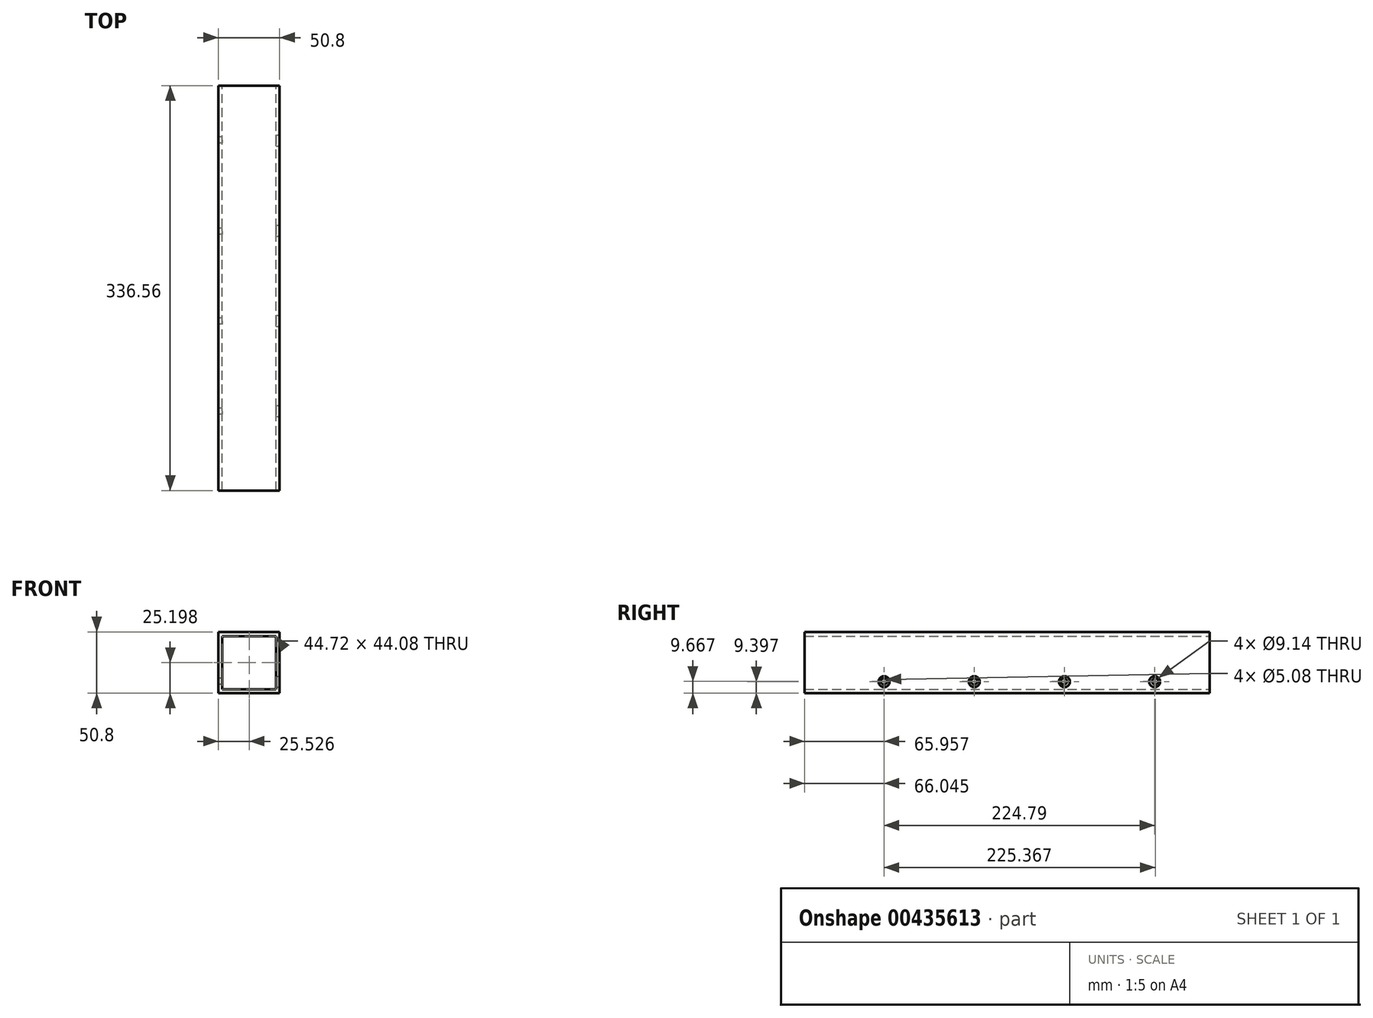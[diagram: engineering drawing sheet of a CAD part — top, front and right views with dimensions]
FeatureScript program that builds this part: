
annotation { "Feature Type Name" : "Feature", "Feature Type Description" : "" }
export const myFeature = defineFeature(function(context is Context, id is Id, definition is map)
    precondition{}
    {
        {
            var Q0;
            Q0=qCreatedBy(makeId("Front.planeOp"),FACE);
            var sketch = newSketch(context, id + "F0", { "sketchPlane" : qUnion([Q0])});
            skLineSegment(sketch, "E0.bottom", {"start": v(-21.26, 25.5) * mm, "end": v(23.47, 25.5) * mm});
            skLineSegment(sketch, "E0.top", {"start": v(-21.26, -18.57) * mm, "end": v(23.47, -18.57) * mm});
            skLineSegment(sketch, "E0.left", {"start": v(-21.26, 25.5) * mm, "end": v(-21.26, -18.57) * mm});
            skLineSegment(sketch, "E0.right", {"start": v(23.47, 25.5) * mm, "end": v(23.47, -18.57) * mm});
            skLineSegment(sketch, "E1.bottom", {"start": v(-24.42, 29.07) * mm, "end": v(26.38, 29.07) * mm});
            skLineSegment(sketch, "E1.top", {"start": v(-24.42, -21.73) * mm, "end": v(26.38, -21.73) * mm});
            skLineSegment(sketch, "E1.left", {"start": v(-24.42, 29.07) * mm, "end": v(-24.42, -21.73) * mm});
            skLineSegment(sketch, "E1.right", {"start": v(26.38, 29.07) * mm, "end": v(26.38, -21.73) * mm});
            skSolve(sketch);
        }
        {
            var Q0;
            Q0=makeQuery(id+"F0.imprint","IMPRINT",FACE,{"disambiguationData":[TD([[makeQuery(id+"F0.imprint","IMPRINT",EDGE,{"derivedFrom":sQuery(id+"F0.wireOp",EDGE,"E0.bottom")}),1.0]])]});
            extrude(context, id + "F1", {"entities" : qUnion([Q0]), "depth" : 336.55 * mm, "symmetric" : true});
        }
        {
            var Q0;
            Q0=makeQuery(id+"F1.opExtrude","SWEPT_FACE",FACE,{"disambiguationData":[OSD([sQuery(id+"F0.wireOp",EDGE,"E1.right")])]});
            var sketch = newSketch(context, id + "F2", { "sketchPlane" : qUnion([Q0])});
            skPoint(sketch, "E2", {"position": v(-102.23, -12.33) * mm});
            skPoint(sketch, "E3", {"position": v(-27.3, -12.33) * mm});
            skPoint(sketch, "E4", {"position": v(47.63, -12.33) * mm});
            skPoint(sketch, "E5", {"position": v(122.56, -12.33) * mm});
            skSolve(sketch);
        }
        {
            var Q0;
            Q0=sQuery(id+"F2.wireOp",VERTEX,"E2");
            var Q1;
            Q1=sQuery(id+"F2.wireOp",VERTEX,"E3");
            var Q2;
            Q2=sQuery(id+"F2.wireOp",VERTEX,"E4");
            var Q3;
            Q3=sQuery(id+"F2.wireOp",VERTEX,"E5");
            var Q4;
            Q4=makeQuery(id+"F1.opExtrude","SWEPT_BODY",BODY,{"disambiguationData":[OSD([sQuery(id+"F0.wireOp",EDGE,"E0.bottom"),sQuery(id+"F0.wireOp",EDGE,"E0.top"),sQuery(id+"F0.wireOp",EDGE,"E0.left"),sQuery(id+"F0.wireOp",EDGE,"E0.right"),sQuery(id+"F0.wireOp",EDGE,"E1.bottom"),sQuery(id+"F0.wireOp",EDGE,"E1.top"),sQuery(id+"F0.wireOp",EDGE,"E1.left"),sQuery(id+"F0.wireOp",EDGE,"E1.right")])]});
            hole(context, id + "F3", {"style" : HoleStyle.SIMPLE, "endStyle" : HoleEndStyle.BLIND, "holeDiameter" : 9.14 * mm, "holeDepth" : 25.4 * mm, "isTappedThrough" : true, "tappedDepth" : 12.7 * mm, "tapClearance" : 3, "locations" : qUnion([Q0, Q1, Q2, Q3]), "scope" : qUnion([Q4])});
        }
        {
            var Q0;
            Q0=makeQuery(id+"F1.opExtrude","SWEPT_FACE",FACE,{"disambiguationData":[OSD([sQuery(id+"F0.wireOp",EDGE,"E1.left")])]});
            var sketch = newSketch(context, id + "F4", { "sketchPlane" : qUnion([Q0])});
            skPoint(sketch, "E6", {"position": v(-123.04, -12.06) * mm});
            skPoint(sketch, "E7", {"position": v(-47.26, -12.06) * mm});
            skPoint(sketch, "E8", {"position": v(27.4, -12.06) * mm});
            skPoint(sketch, "E9", {"position": v(102.32, -12.06) * mm});
            skSolve(sketch);
        }
        {
            var Q0;
            Q0=sQuery(id+"F4.wireOp",VERTEX,"E6");
            var Q1;
            Q1=sQuery(id+"F4.wireOp",VERTEX,"E7");
            var Q2;
            Q2=sQuery(id+"F4.wireOp",VERTEX,"E8");
            var Q3;
            Q3=sQuery(id+"F4.wireOp",VERTEX,"E9");
            var Q4;
            Q4=makeQuery(id+"F1.opExtrude","SWEPT_BODY",BODY,{"disambiguationData":[OSD([sQuery(id+"F0.wireOp",EDGE,"E0.bottom"),sQuery(id+"F0.wireOp",EDGE,"E0.top"),sQuery(id+"F0.wireOp",EDGE,"E0.left"),sQuery(id+"F0.wireOp",EDGE,"E0.right"),sQuery(id+"F0.wireOp",EDGE,"E1.bottom"),sQuery(id+"F0.wireOp",EDGE,"E1.top"),sQuery(id+"F0.wireOp",EDGE,"E1.left"),sQuery(id+"F0.wireOp",EDGE,"E1.right")])]});
            hole(context, id + "F5", {"style" : HoleStyle.SIMPLE, "endStyle" : HoleEndStyle.BLIND, "holeDiameter" : 5.08 * mm, "holeDepth" : 25.4 * mm, "isTappedThrough" : true, "tappedDepth" : 12.7 * mm, "tapClearance" : 3, "locations" : qUnion([Q0, Q1, Q2, Q3]), "scope" : qUnion([Q4])});
        }
    });
